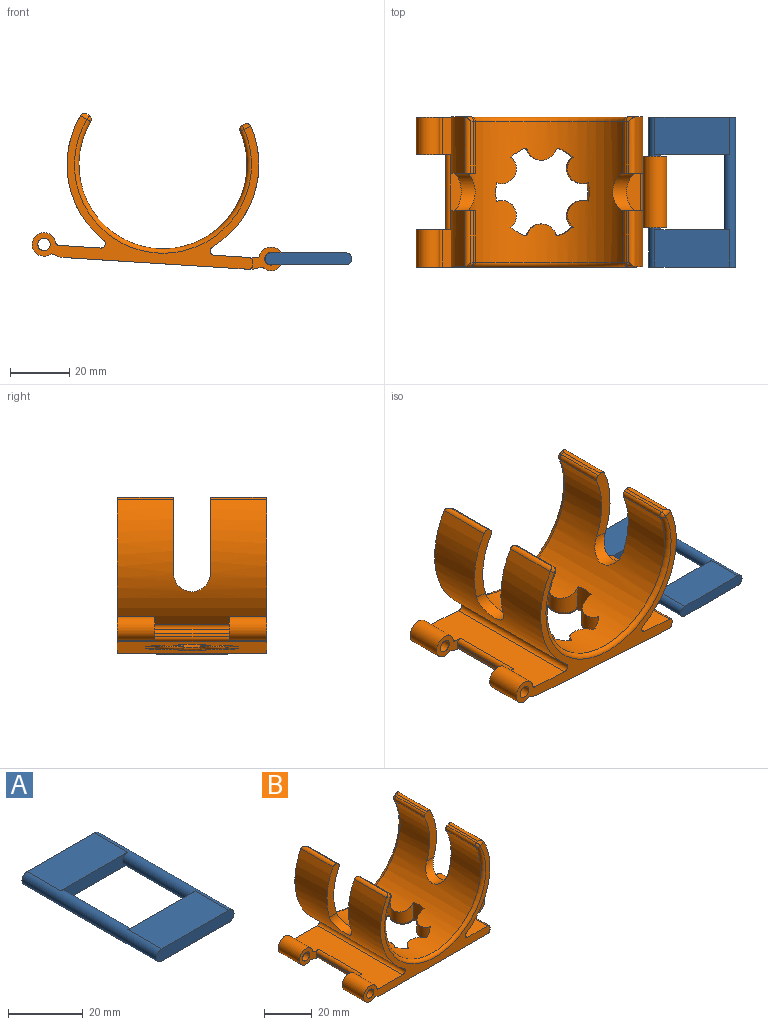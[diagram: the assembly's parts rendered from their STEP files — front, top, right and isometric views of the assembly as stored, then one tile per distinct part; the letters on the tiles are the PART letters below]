
ASSEMBLY  parts=2 mates=1
PART A: 12 faces, bbox 29.4x50.8x4 mm
  f0: plane 12.7x0mm, normal (1,0,0), area 0mm2, adj f1,f3,f9,f10
  f1: plane 25.36x12.7mm, normal (0,0,1), area 322.1mm2, adj f0,f6,f9,f10
  f2: plane 25.36x12.7mm, normal (0,0,-1), area 322.1mm2, adj f3,f6,f9,f10
  f3: cylinder r=2mm len=50.8mm, axis (0,1,0), area 480.7mm2, adj f0,f2,f4,f7,f8,f9,f10,f11
  f4: plane 12.7x0mm, normal (1,0,0), area 0mm2, adj f3,f5,f8,f11
  f5: plane 25.36x12.7mm, normal (0,0,1), area 322.1mm2, adj f4,f6,f8,f11
  f6: cylinder r=2mm len=50.8mm, axis (0,1,0), area 478.7mm2, adj f1,f2,f5,f7,f8,f9,f10,f11
  f7: plane 25.36x12.7mm, normal (0,0,-1), area 322.1mm2, adj f3,f6,f8,f11
  f8: plane 29.4x4mm, normal (0,-1,0), area 114.2mm2, adj f3,f4,f5,f6,f7
  f9: plane 29.4x4mm, normal (0,1,0), area 114.2mm2, adj f0,f1,f2,f3,f6
  f10: plane 25.36x4mm, normal (0,-1,0), area 89mm2, adj f0,f1,f2,f3,f6
  f11: plane 25.36x4mm, normal (0,1,0), area 89mm2, adj f3,f4,f5,f6,f7
PART B: 99 faces, bbox 85x50.8x49.9 mm
  f0: cylinder r=28.5mm len=57mm, axis (0,1,0), area 4242.3mm2, adj f6,f8,f34,f40,f41,f45,f54,f55
  f1: plane 17.55x0.87mm, normal (-0.5,0,0.87), area 17.6mm2, adj f7,f8,f39,f75
  f2: plane 17.55x0.87mm, normal (0.5,0,0.87), area 17.6mm2, adj f5,f6,f33,f79
  f3: cylinder r=32.5mm len=50.8mm, axis (0,1,0), area 1987.9mm2, adj f5,f19,f20,f32,f52,f78,f79,f80
  f4: cylinder r=32.5mm len=50.8mm, axis (0,1,0), area 1987.8mm2, adj f7,f19,f20,f38,f53,f75,f76,f77
  f5: cylinder r=1.5mm len=19.05mm, axis (0,1,0), area 45mm2, adj f2,f3,f19,f33,f79
  f6: cylinder r=1.5mm len=17.55mm, axis (0,1,0), area 40mm2, adj f0,f2,f36,f79
  f7: cylinder r=1.5mm len=19.05mm, axis (0,1,0), area 45mm2, adj f1,f4,f19,f39,f75
  f8: cylinder r=1.5mm len=17.55mm, axis (0,1,0), area 40mm2, adj f0,f1,f43,f75
  f9: plane 64.1x50.8mm, normal (0,0,-1), area 2508.9mm2, adj f19,f20,f24,f25,f30,f31,f47,f48
  f10: plane 13.34x1mm, normal (1,0,0), area 13.3mm2, adj f20,f31,f46,f47
  f11: plane 50.8x14.31mm, normal (0,0,1), area 661.1mm2, adj f19,f20,f24,f25,f49,f52,f73,f74
  f12: cylinder r=4mm len=12.7mm, axis (0,1,0), area 266mm2, adj f13,f20,f24,f73
  f13: plane 12.7x2.63mm, normal (-0.29,0,-0.96), area 34.9mm2, adj f12,f20,f24,f97
  f14: cylinder r=2.1mm len=12.7mm, axis (0,1,0), area 167.6mm2, adj f20,f24
  f15: plane 17.55x0.87mm, normal (-0.5,0,0.87), area 17.6mm2, adj f38,f42,f45,f76
  f16: plane 17.55x0.87mm, normal (0.5,0,0.87), area 17.6mm2, adj f32,f34,f35,f80
  f17: plane 13.34x1mm, normal (1,0,0), area 13.3mm2, adj f19,f30,f50,f51
  f18: plane 50.8x14.31mm, normal (0,0,1), area 657.8mm2, adj f19,f20,f30,f31,f46,f50,f53,f72
  f19: plane 75x48.43mm, normal (0,-1,0), area 579.3mm2, adj f3,f4,f5,f7,f9,f11,f17,f18
  f20: plane 75x48.43mm, normal (0,1,0), area 579.3mm2, adj f3,f4,f9,f10,f11,f12,f13,f14
  f21: cylinder r=4mm len=12.7mm, axis (0,1,0), area 266mm2, adj f19,f22,f25,f74
  f22: plane 12.7x2.63mm, normal (-0.29,0,-0.96), area 34.9mm2, adj f19,f21,f25,f98
  f23: cylinder r=2.1mm len=12.7mm, axis (0,1,0), area 167.6mm2, adj f19,f25
  f24: plane 11.5x8mm, normal (0,-1,0), area 46.4mm2, adj f9,f11,f12,f13,f14,f26,f48,f49
  f25: plane 11.5x8mm, normal (0,1,0), area 46.4mm2, adj f9,f11,f21,f22,f23,f26,f48,f49
  f26: plane 25.4x1mm, normal (-1,0,0), area 25.4mm2, adj f24,f25,f48,f49
  f27: plane 24.13x2.71mm, normal (0.29,0,-0.96), area 68.2mm2, adj f30,f31,f70,f71
  f28: cylinder r=4mm len=24.13mm, axis (0,1,0), area 494.2mm2, adj f30,f31,f71,f72
  f29: cylinder r=2.1mm len=24.13mm, axis (0,1,0), area 318.4mm2, adj f30,f31
  f30: plane 11.5x8mm, normal (0,-1,0), area 46.5mm2, adj f9,f17,f18,f27,f28,f29,f50,f51
  f31: plane 11.5x8mm, normal (0,1,0), area 46.5mm2, adj f9,f10,f18,f27,f28,f29,f46,f47
  f32: cylinder r=1.5mm len=19.05mm, axis (0,1,0), area 45mm2, adj f3,f16,f20,f35,f80
  f33: cylinder r=1.5mm len=2.92mm, axis (0.87,0,-0.5), area 4.6mm2, adj f2,f5,f19,f36
  f34: cylinder r=1.5mm len=17.55mm, axis (0,1,0), area 40mm2, adj f0,f16,f37,f80
  f35: cylinder r=1.5mm len=2.92mm, axis (-0.87,0,0.5), area 4.6mm2, adj f16,f20,f32,f37
  f36: sphere r=1.5mm, area 3.4mm2, adj f6,f33,f40
  f37: sphere r=1.5mm, area 3.4mm2, adj f34,f35,f41
  f38: cylinder r=1.5mm len=19.05mm, axis (0,1,0), area 45mm2, adj f4,f15,f20,f42,f76
  f39: cylinder r=1.5mm len=2.92mm, axis (0.87,0,0.5), area 4.6mm2, adj f1,f7,f19,f43
  f40: torus R=30mm, axis (0,-1,0), area 279.8mm2, adj f0,f19,f36,f43
  f41: torus R=30mm, axis (0,-1,0), area 279.8mm2, adj f0,f20,f37,f44
  f42: cylinder r=1.5mm len=2.92mm, axis (-0.87,0,-0.5), area 4.6mm2, adj f15,f20,f38,f44
  f43: sphere r=1.5mm, area 3.4mm2, adj f8,f39,f40
  f44: sphere r=1.5mm, area 3.4mm2, adj f41,f42,f45
  f45: cylinder r=1.5mm len=17.55mm, axis (0,1,0), area 40mm2, adj f0,f15,f44,f76
  f46: cylinder r=1.5mm len=13.34mm, axis (0,1,0), area 31.4mm2, adj f10,f18,f20,f31
  f47: cylinder r=1.5mm len=13.34mm, axis (0,-1,0), area 31.4mm2, adj f9,f10,f20,f31
  f48: cylinder r=1.5mm len=25.4mm, axis (0,1,0), area 59.8mm2, adj f9,f24,f25,f26
  f49: cylinder r=1.5mm len=25.4mm, axis (0,-1,0), area 59.8mm2, adj f11,f24,f25,f26
  f50: cylinder r=1.5mm len=13.34mm, axis (0,1,0), area 31.4mm2, adj f17,f18,f19,f30
  f51: cylinder r=1.5mm len=13.34mm, axis (0,-1,0), area 31.4mm2, adj f9,f17,f19,f30
  f52: cylinder r=1.5mm len=50.8mm, axis (0,1,0), area 193.4mm2, adj f3,f11,f19,f20
  f53: cylinder r=1.5mm len=50.8mm, axis (0,1,0), area 193.4mm2, adj f4,f18,f19,f20
  f54: cylinder r=5.08mm len=9.51mm, axis (0,0,-1), area 51.3mm2, adj f0,f66,f69,f82
  f55: cylinder r=15.88mm len=6.02mm, axis (0,0,-1), area 28mm2, adj f0,f56,f66,f83
  f56: cylinder r=5.08mm len=9.02mm, axis (0,0,-1), area 88.3mm2, adj f0,f55,f57,f85
  f57: cylinder r=15.88mm len=8.83mm, axis (0,0,-1), area 56.2mm2, adj f0,f56,f58,f87
  f58: cylinder r=5.08mm len=9.02mm, axis (0,0,-1), area 88.3mm2, adj f0,f57,f59,f89
  f59: cylinder r=15.88mm len=6.02mm, axis (0,0,-1), area 28mm2, adj f0,f58,f67,f91
  f60: cylinder r=5.08mm len=9.51mm, axis (0,0,-1), area 51.3mm2, adj f0,f67,f68,f95
  f61: cylinder r=15.88mm len=6.02mm, axis (0,0,-1), area 28mm2, adj f0,f62,f68,f94
  f62: cylinder r=5.08mm len=9.02mm, axis (0,0,-1), area 88.3mm2, adj f0,f61,f63,f92
  f63: cylinder r=15.88mm len=8.83mm, axis (0,0,-1), area 56.2mm2, adj f0,f62,f64,f90
  f64: cylinder r=5.08mm len=9.02mm, axis (0,0,-1), area 88.3mm2, adj f0,f63,f65,f88
  f65: cylinder r=15.88mm len=6.02mm, axis (0,0,-1), area 28mm2, adj f0,f64,f69,f86
  f66: cylinder r=1mm len=4.66mm, axis (0,0,-1), area 7.3mm2, adj f0,f54,f55,f81
  f67: cylinder r=1mm len=4.66mm, axis (0,0,-1), area 7.3mm2, adj f0,f59,f60,f93
  f68: cylinder r=1mm len=4.66mm, axis (0,0,-1), area 7.3mm2, adj f0,f60,f61,f96
  f69: cylinder r=1mm len=4.66mm, axis (0,0,-1), area 7.3mm2, adj f0,f54,f65,f84
  f70: cylinder r=1mm len=24.13mm, axis (0,-1,0), area 7.1mm2, adj f9,f27,f30,f31
  f71: cylinder r=1mm len=24.13mm, axis (0,1,0), area 21.8mm2, adj f27,f28,f30,f31
  f72: cylinder r=1mm len=24.13mm, axis (0,1,0), area 33mm2, adj f18,f28,f30,f31
  f73: cylinder r=1mm len=12.7mm, axis (0,1,0), area 17.4mm2, adj f11,f12,f20,f24
  f74: cylinder r=1mm len=12.7mm, axis (0,1,0), area 17.4mm2, adj f11,f19,f21,f25
  f75: plane 25.68x7.3mm, normal (0,1,0), area 103.7mm2, adj f0,f1,f4,f7,f8,f77
  f76: plane 25.68x7.3mm, normal (0,-1,0), area 103.7mm2, adj f0,f4,f15,f38,f45,f77
  f77: cylinder r=6.35mm len=12.7mm, axis (1,0,0), area 90.4mm2, adj f0,f4,f75,f76
  f78: cylinder r=6.35mm len=12.7mm, axis (1,0,0), area 90.4mm2, adj f0,f3,f79,f80
  f79: plane 25.68x7.3mm, normal (0,1,0), area 103.7mm2, adj f0,f2,f3,f5,f6,f78
  f80: plane 25.68x7.3mm, normal (0,-1,0), area 103.7mm2, adj f0,f3,f16,f32,f34,f78
  f81: torus R=2mm, axis (0,0,1), area 3.4mm2, adj f9,f66,f82,f83
  f82: torus R=4.08mm, axis (0,0,1), area 18mm2, adj f9,f54,f81,f84
  f83: torus R=16.88mm, axis (0,0,1), area 9.2mm2, adj f9,f55,f81,f85
  f84: torus R=2mm, axis (0,0,1), area 3.4mm2, adj f9,f69,f82,f86
  f85: torus R=4.08mm, axis (0,0,1), area 22.2mm2, adj f9,f56,f83,f87
  f86: torus R=16.88mm, axis (0,0,1), area 9.2mm2, adj f9,f65,f84,f88
  f87: torus R=16.88mm, axis (0,0,1), area 11.8mm2, adj f9,f57,f85,f89
  f88: torus R=4.08mm, axis (0,0,1), area 22.2mm2, adj f9,f64,f86,f90
  f89: torus R=4.08mm, axis (0,0,1), area 22.2mm2, adj f9,f58,f87,f91
  f90: torus R=16.88mm, axis (0,0,1), area 11.8mm2, adj f9,f63,f88,f92
  f91: torus R=16.88mm, axis (0,0,1), area 9.2mm2, adj f9,f59,f89,f93
  f92: torus R=4.08mm, axis (0,0,1), area 22.2mm2, adj f9,f62,f90,f94
  f93: torus R=2mm, axis (0,0,1), area 3.4mm2, adj f9,f67,f91,f95
  f94: torus R=16.88mm, axis (0,0,1), area 9.2mm2, adj f9,f61,f92,f96
  f95: torus R=4.08mm, axis (0,0,1), area 18mm2, adj f9,f60,f93,f96
  f96: torus R=2mm, axis (0,0,1), area 3.4mm2, adj f9,f68,f94,f95
  f97: cylinder r=5.08mm len=12.7mm, axis (0,1,0), area 18.9mm2, adj f9,f13,f20,f24
  f98: cylinder r=5.08mm len=12.7mm, axis (0,1,0), area 18.9mm2, adj f9,f19,f22,f25
PLACE A t=(84.51,-7.25,9.57)mm fixed
PLACE B rot(axis=(0,1,0),3.6deg) t=(-15.95,-7.25,11.95)mm
MATE revolute B.f28 <-> A.f6  axis (0,1,0) through (20.61,-7.25,-19.93)mm
